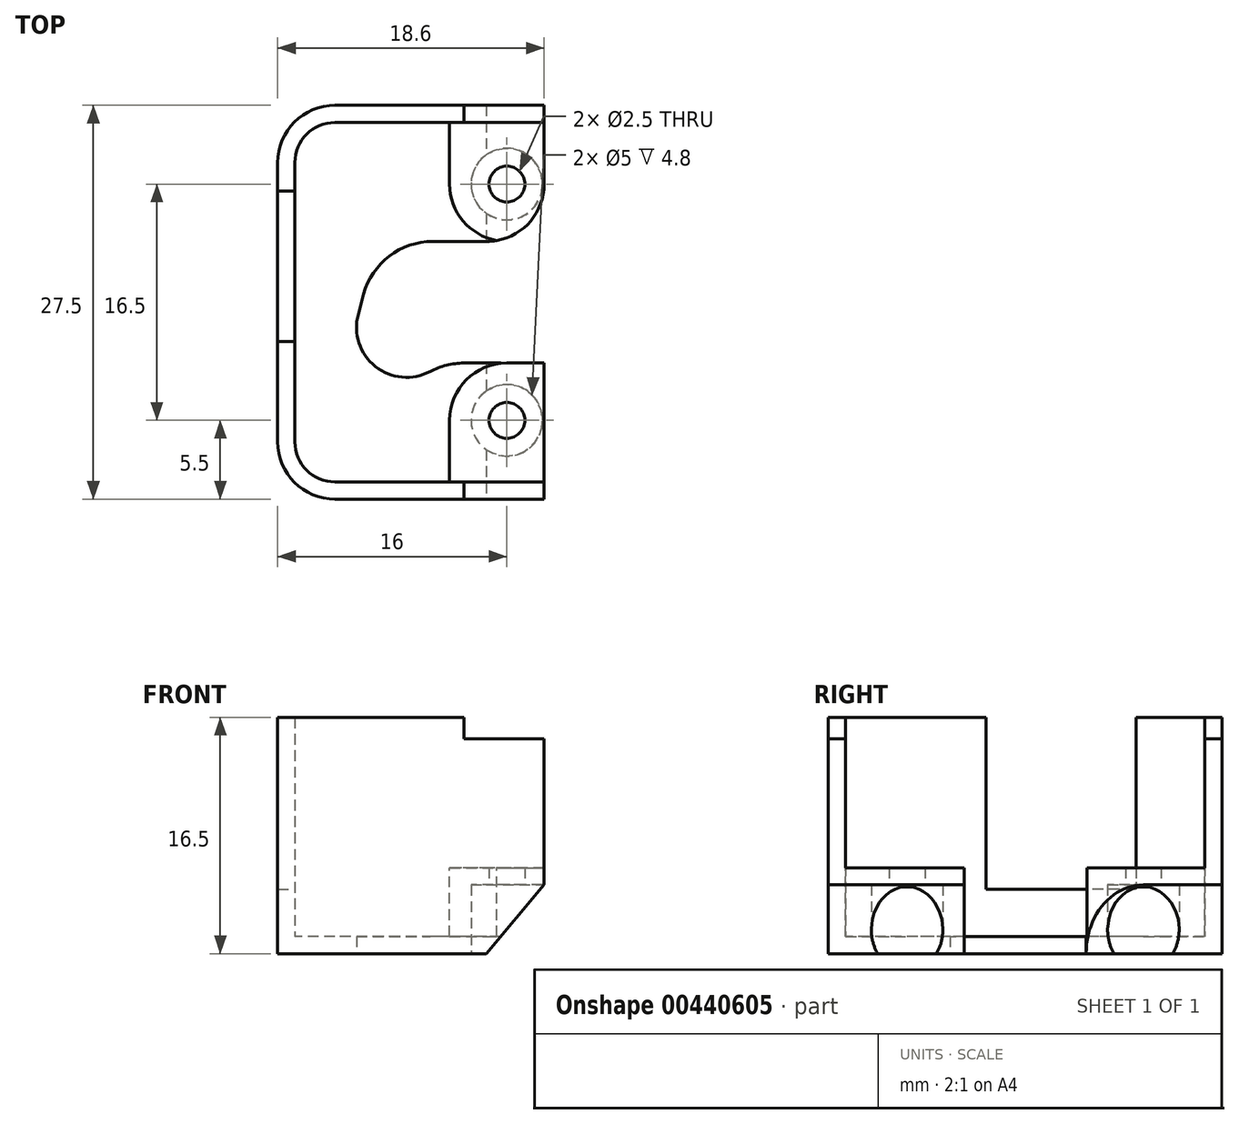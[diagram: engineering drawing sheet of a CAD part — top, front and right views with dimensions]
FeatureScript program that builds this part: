
annotation { "Feature Type Name" : "Feature", "Feature Type Description" : "" }
export const myFeature = defineFeature(function(context is Context, id is Id, definition is map)
    precondition{}
    {
        {
            var Q0;
            Q0=qCreatedBy(makeId("Top.planeOp"),FACE);
            var sketch = newSketch(context, id + "F0", { "sketchPlane" : qUnion([Q0])});
            skCircle(sketch, "E0", {"center": v(0, 8.25) * mm, "radius": 1.25 * mm});
            skCircle(sketch, "E1", {"center": v(0, -8.25) * mm, "radius": 1.25 * mm});
            skCircle(sketch, "E2", {"center": v(37.5, 11) * mm, "radius": 1.25 * mm});
            skCircle(sketch, "E3", {"center": v(37.5, -11) * mm, "radius": 1.25 * mm});
            skSolve(sketch);
        }
        {
            var Q0;
            Q0=qCreatedBy(makeId("Top.planeOp"),FACE);
            var sketch = newSketch(context, id + "F1", { "sketchPlane" : qUnion([Q0])});
            skLineSegment(sketch, "E4.bottom", {"start": v(-4, 12.25) * mm, "end": v(33.5, 12.25) * mm});
            skLineSegment(sketch, "E4.top", {"start": v(-4, -12.25) * mm, "end": v(33.5, -12.25) * mm});
            skLineSegment(sketch, "E4.left", {"start": v(-4, 12.25) * mm, "end": v(-4, -12.25) * mm});
            skLineSegment(sketch, "E4.right", {"start": v(43.5, 15) * mm, "end": v(43.5, -15) * mm});
            skCircle(sketch, "E5", {"center": v(37.5, 11) * mm, "radius": 2.5 * mm, "construction": true});
            skCircle(sketch, "E6", {"center": v(37.5, -11) * mm, "radius": 2.5 * mm, "construction": true});
            skCircle(sketch, "E7", {"center": v(0, 8.25) * mm, "radius": 2.5 * mm});
            skCircle(sketch, "E8", {"center": v(0, -8.25) * mm, "radius": 2.5 * mm});
            skLineSegment(sketch, "E9", {"start": v(33.5, 15) * mm, "end": v(43.5, 15) * mm});
            skLineSegment(sketch, "E10", {"start": v(33.5, -15) * mm, "end": v(43.5, -15) * mm});
            skLineSegment(sketch, "E11", {"start": v(33.5, 12.25) * mm, "end": v(33.5, 15) * mm});
            skLineSegment(sketch, "E12", {"start": v(33.5, -12.25) * mm, "end": v(33.5, -15) * mm});
            skSolve(sketch);
        }
        {
            var Q0;
            Q0=qCreatedBy(makeId("Top.planeOp"),FACE);
            var sketch = newSketch(context, id + "F2", { "sketchPlane" : qUnion([Q0])});
            skCircle(sketch, "E13", {"center": v(0, 8.25) * mm, "radius": 2.5 * mm, "construction": true});
            skLineSegment(sketch, "E14.bottom", {"start": v(2.6, 13.75) * mm, "end": v(-16, 13.75) * mm});
            skLineSegment(sketch, "E14.top", {"start": v(2.6, -13.75) * mm, "end": v(-16, -13.75) * mm});
            skLineSegment(sketch, "E14.left", {"start": v(2.6, 13.75) * mm, "end": v(2.6, 4.25) * mm});
            skLineSegment(sketch, "E14.right", {"start": v(-16, 13.75) * mm, "end": v(-16, -13.75) * mm});
            skLineSegment(sketch, "E15.bottom", {"start": v(2.6, -4.25) * mm, "end": v(-4.55, -4.25) * mm});
            skLineSegment(sketch, "E15.top", {"start": v(2.6, 4.25) * mm, "end": v(-9, 4.25) * mm});
            skLineSegment(sketch, "E16.trimOffspring", {"start": v(2.6, -4.25) * mm, "end": v(2.6, -13.75) * mm});
            skArc(sketch, "E17", {"start": v(-10.38, -0.83) * mm, "mid": v(-8.77, -4.77) * mm, "end": v(-4.55, -4.25) * mm});
            skLineSegment(sketch, "E18", {"start": v(-9, 4.25) * mm, "end": v(-10.38, -0.83) * mm});
            skSolve(sketch);
        }
        {
            var Q0;
            Q0=qCreatedBy(makeId("Top.planeOp"),FACE);
            var sketch = newSketch(context, id + "F3", { "sketchPlane" : qUnion([Q0])});
            skLineSegment(sketch, "E19.bottom", {"start": v(2.6, -4.25) * mm, "end": v(-5.4, -4.25) * mm});
            skLineSegment(sketch, "E19.top", {"start": v(2.6, 4.25) * mm, "end": v(-5.4, 4.25) * mm});
            skLineSegment(sketch, "E19.right", {"start": v(-5.4, -4.25) * mm, "end": v(-5.4, 4.25) * mm});
            skLineSegment(sketch, "E20", {"start": v(2.6, -4.25) * mm, "end": v(2.6, 4.25) * mm});
            skSolve(sketch);
        }
        {
            var Q0;
            Q0=makeQuery(id+"F2.imprint","IMPRINT",FACE,{"disambiguationData":[TD([[makeQuery(id+"F2.imprint","IMPRINT",EDGE,{"derivedFrom":sQuery(id+"F2.wireOp",EDGE,"E14.bottom")}),1.0]])]});
            var Q1;
            {var subQ0=sQuery(id+"F2.wireOp",EDGE,"E15.right");var subQ1=sQuery(id+"F2.wireOp",EDGE,"E15.bottom");var subQ2=makeQuery(id+"F2.imprint","INTERSECT",VERTEX,{"derivedFrom":[subQ1,subQ0]});Q1=makeQuery(id+"F2.imprint","IMPRINT",FACE,{"disambiguationData":[TD([[makeQuery(id+"F2.imprint","IMPRINT",EDGE,{"disambiguationData":[TD([[subQ2,1.0]])],"derivedFrom":subQ1}),-1.0]])]});}
            extrude(context, id + "F4", {"entities" : qUnion([Q0, Q1]), "depth" : 13.5 * mm, "hasSecondDirection" : true, "secondDirectionOppositeDirection" : true, "secondDirectionDepth" : 3 * mm});
        }
        {
            var Q0;
            Q0=makeQuery(id+"F4.opExtrude","SWEPT_EDGE",EDGE,{"disambiguationData":[OSD([sQuery(id+"F2.wireOp",EDGE,"E14.bottom"),sQuery(id+"F2.wireOp",EDGE,"E14.right")])]});
            var Q1;
            Q1=makeQuery(id+"F4.opExtrude","SWEPT_EDGE",EDGE,{"disambiguationData":[OSD([sQuery(id+"F2.wireOp",EDGE,"E14.top"),sQuery(id+"F2.wireOp",EDGE,"E14.right")])]});
            fillet(context, id + "F5", {"entities" : qUnion([Q0, Q1]), "radius" : 4 * mm, "tangentPropagation" : true, "allowEdgeOverflow" : false});
        }
        {
            var Q0;
            Q0=makeQuery(id+"F4.opExtrude","CAP_FACE",FACE,{"disambiguationData":[OSD([sQuery(id+"F2.wireOp",EDGE,"E14.bottom"),sQuery(id+"F2.wireOp",EDGE,"E14.top"),sQuery(id+"F2.wireOp",EDGE,"E14.left"),sQuery(id+"F2.wireOp",EDGE,"E14.right"),sQuery(id+"F2.wireOp",EDGE,"E15.bottom"),sQuery(id+"F2.wireOp",EDGE,"E15.top"),sQuery(id+"F2.wireOp",EDGE,"E15.right"),sQuery(id+"F2.wireOp",EDGE,"E16.trimOffspring")])],"isStart":false});
            var Q1;
            Q1=makeQuery(id+"F4.opExtrude","SWEPT_FACE",FACE,{"disambiguationData":[OSD([sQuery(id+"F2.wireOp",EDGE,"E14.left")])]});
            var Q2;
            Q2=makeQuery(id+"F4.opExtrude","SWEPT_FACE",FACE,{"disambiguationData":[OSD([sQuery(id+"F2.wireOp",EDGE,"E16.trimOffspring")])]});
            var Q3;
            Q3=makeQuery(id+"F4.opExtrude","SWEPT_FACE",FACE,{"disambiguationData":[OSD([sQuery(id+"F2.wireOp",EDGE,"E15.right")])]});
            var Q4;
            Q4=makeQuery(id+"F4.opExtrude","SWEPT_FACE",FACE,{"disambiguationData":[OSD([sQuery(id+"F2.wireOp",EDGE,"E15.bottom")])]});
            var Q5;
            Q5=makeQuery(id+"F4.opExtrude","SWEPT_FACE",FACE,{"disambiguationData":[OSD([sQuery(id+"F2.wireOp",EDGE,"E15.top")])]});
            var Q6;
            {var subQ1=sQuery(id+"F2.wireOp",EDGE,"E14.top");Q6=makeQuery(id+"F8.boolean.opBoolean","COPY",FACE,{"disambiguationData":[TD([makeQuery(id+"F4.opExtrude","SWEPT_FACE",FACE,{"disambiguationData":[OSD([subQ1])]})])],"derivedFrom":makeQuery(id+"F8.opExtrude","SWEPT_FACE",FACE,{"disambiguationData":[OSD([sQuery(id+"F7.wireOp",EDGE,"E21.right")])]})});}
            var Q7;
            {var subQ0=sQuery(id+"F2.wireOp",EDGE,"E14.bottom");Q7=makeQuery(id+"F8.boolean.opBoolean","COPY",FACE,{"disambiguationData":[TD([makeQuery(id+"F4.opExtrude","SWEPT_FACE",FACE,{"disambiguationData":[OSD([subQ0])]})])],"derivedFrom":makeQuery(id+"F8.opExtrude","SWEPT_FACE",FACE,{"disambiguationData":[OSD([sQuery(id+"F7.wireOp",EDGE,"E21.right")])]})});}
            var Q8;
            Q8=makeQuery(id+"F4.opExtrude","SWEPT_FACE",FACE,{"disambiguationData":[OSD([sQuery(id+"F2.wireOp",EDGE,"E17")])]});
            var Q9;
            Q9=makeQuery(id+"F4.opExtrude","SWEPT_FACE",FACE,{"disambiguationData":[OSD([sQuery(id+"F2.wireOp",EDGE,"E18")])]});
            shell(context, id + "F6", {"entities" : qUnion([Q0, Q1, Q2, Q3, Q4, Q5, Q6, Q7, Q8, Q9]), "thickness" : 1.2 * mm});
        }
        {
            var Q0;
            Q0=qCreatedBy(makeId("Front.planeOp"),FACE);
            var sketch = newSketch(context, id + "F7", { "sketchPlane" : qUnion([Q0])});
            skLineSegment(sketch, "E21.bottom", {"start": v(2.6, -3) * mm, "end": v(-4, -3) * mm});
            skLineSegment(sketch, "E21.top", {"start": v(2.6, 3) * mm, "end": v(-4, 3) * mm});
            skLineSegment(sketch, "E21.left", {"start": v(2.6, -3) * mm, "end": v(2.6, 3) * mm});
            skLineSegment(sketch, "E21.right", {"start": v(-4, -3) * mm, "end": v(-4, 3) * mm});
            skSolve(sketch);
        }
        {
            var Q0;
            Q0=makeQuery(id+"F7.imprint","IMPRINT",FACE,{"disambiguationData":[TD([[makeQuery(id+"F7.imprint","IMPRINT",EDGE,{"derivedFrom":sQuery(id+"F7.wireOp",EDGE,"E21.bottom")}),-1.0]])]});
            var Q1;
            Q1=makeQuery(id+"F4.opExtrude","SWEPT_FACE",FACE,{"disambiguationData":[OSD([sQuery(id+"F2.wireOp",EDGE,"E14.bottom")])]});
            var Q2;
            Q2=makeQuery(id+"F4.opExtrude","SWEPT_FACE",FACE,{"disambiguationData":[OSD([sQuery(id+"F2.wireOp",EDGE,"E14.top")])]});
            extrude(context, id + "F8", {"entities" : qUnion([Q0]), "operationType" : NewBodyOperationType.ADD, "endBound" : BoundingType.UP_TO_SURFACE, "oppositeDirection" : true, "endBoundEntityFace" : qUnion([Q1]), "depth" : 13 * mm, "hasSecondDirection" : true, "secondDirectionBound" : SecondDirectionBoundingType.UP_TO_SURFACE, "secondDirectionOppositeDirection" : false, "secondDirectionBoundEntityFace" : qUnion([Q2]), "secondDirectionDepth" : 25 * mm});
        }
        {
            var Q0;
            Q0=makeQuery(id+"F3.imprint","IMPRINT",FACE,{"disambiguationData":[TD([[makeQuery(id+"F3.imprint","IMPRINT",EDGE,{"derivedFrom":sQuery(id+"F3.wireOp",EDGE,"E19.bottom")}),-1.0]])]});
            extrude(context, id + "F9", {"entities" : qUnion([Q0]), "operationType" : NewBodyOperationType.REMOVE, "depth" : 4.5 * mm, "hasSecondDirection" : true, "secondDirectionOppositeDirection" : true, "secondDirectionDepth" : 4.3 * mm});
        }
        {
            var Q0;
            Q0=qCreatedBy(makeId("Right.planeOp"),FACE);
            var sketch = newSketch(context, id + "F10", { "sketchPlane" : qUnion([Q0])});
            skLineSegment(sketch, "E22.bottom", {"start": v(7.75, 19.94) * mm, "end": v(-2.75, 19.94) * mm});
            skLineSegment(sketch, "E22.top", {"start": v(7.75, 1.5) * mm, "end": v(-2.75, 1.5) * mm});
            skLineSegment(sketch, "E22.left", {"start": v(7.75, 19.94) * mm, "end": v(7.75, 1.5) * mm});
            skLineSegment(sketch, "E22.right", {"start": v(-2.75, 19.94) * mm, "end": v(-2.75, 1.5) * mm});
            skSolve(sketch);
        }
        {
            var Q0;
            Q0 = qSketchRegion(id + "F10", true);
            extrude(context, id + "F11", {"entities" : qUnion([Q0]), "operationType" : NewBodyOperationType.REMOVE, "oppositeDirection" : true, "depth" : 17.9 * mm, "hasSecondDirection" : true, "secondDirectionOppositeDirection" : true, "secondDirectionDepth" : 6.5 * mm});
        }
        {
            var Q0;
            Q0=makeQuery(id+"F9.boolean.opBoolean","COPY",EDGE,{"derivedFrom":makeQuery(id+"F9.opExtrude","SWEPT_EDGE",EDGE,{"disambiguationData":[OSD([sQuery(id+"F3.wireOp",EDGE,"E19.bottom"),sQuery(id+"F3.wireOp",EDGE,"E20")])]})});
            var Q1;
            Q1=makeQuery(id+"F9.boolean.opBoolean","INTERSECT",EDGE,{"derivedFrom":[makeQuery(id+"F8.opExtrude","SWEPT_FACE",FACE,{"disambiguationData":[OSD([sQuery(id+"F7.wireOp",EDGE,"E21.right")])]}),makeQuery(id+"F9.opExtrude","SWEPT_FACE",FACE,{"disambiguationData":[OSD([sQuery(id+"F3.wireOp",EDGE,"E19.bottom")])]})]});
            var Q2;
            Q2=makeQuery(id+"F9.boolean.opBoolean","INTERSECT",EDGE,{"derivedFrom":[makeQuery(id+"F8.opExtrude","SWEPT_FACE",FACE,{"disambiguationData":[OSD([sQuery(id+"F7.wireOp",EDGE,"E21.right")])]}),makeQuery(id+"F9.opExtrude","SWEPT_FACE",FACE,{"disambiguationData":[OSD([sQuery(id+"F3.wireOp",EDGE,"E19.top")])]})]});
            var Q3;
            Q3=makeQuery(id+"F9.boolean.opBoolean","COPY",EDGE,{"derivedFrom":makeQuery(id+"F9.opExtrude","SWEPT_EDGE",EDGE,{"disambiguationData":[OSD([sQuery(id+"F3.wireOp",EDGE,"E19.top"),sQuery(id+"F3.wireOp",EDGE,"E20")])]})});
            fillet(context, id + "F12", {"entities" : qUnion([Q0, Q1, Q2, Q3]), "radius" : 4 * mm, "tangentPropagation" : true, "allowEdgeOverflow" : false});
        }
        {
            var Q0;
            Q0=makeQuery(id+"F0.imprint","IMPRINT",FACE,{"disambiguationData":[TD([[makeQuery(id+"F0.imprint","IMPRINT",EDGE,{"derivedFrom":sQuery(id+"F0.wireOp",EDGE,"E1")}),1.0]])]});
            var Q1;
            Q1=makeQuery(id+"F0.imprint","IMPRINT",FACE,{"disambiguationData":[TD([[makeQuery(id+"F0.imprint","IMPRINT",EDGE,{"derivedFrom":sQuery(id+"F0.wireOp",EDGE,"E0")}),1.0]])]});
            extrude(context, id + "F13", {"entities" : qUnion([Q0, Q1]), "operationType" : NewBodyOperationType.REMOVE, "depth" : 7.9 * mm, "hasSecondDirection" : true, "secondDirectionOppositeDirection" : true, "secondDirectionDepth" : 7.1 * mm});
        }
        {
            var Q0;
            Q0=makeQuery(id+"F1.imprint","IMPRINT",FACE,{"disambiguationData":[TD([[makeQuery(id+"F1.imprint","IMPRINT",EDGE,{"derivedFrom":sQuery(id+"F1.wireOp",EDGE,"E8")}),1.0]])]});
            var Q1;
            Q1=makeQuery(id+"F1.imprint","IMPRINT",FACE,{"disambiguationData":[TD([[makeQuery(id+"F1.imprint","IMPRINT",EDGE,{"derivedFrom":sQuery(id+"F1.wireOp",EDGE,"E7")}),1.0]])]});
            extrude(context, id + "F14", {"entities" : qUnion([Q0, Q1]), "operationType" : NewBodyOperationType.REMOVE, "depth" : 1.8 * mm, "hasSecondDirection" : true, "secondDirectionOppositeDirection" : true, "secondDirectionDepth" : 4.3 * mm});
        }
        {
            var Q0;
            Q0=makeQuery(id+"F4.opExtrude","SWEPT_EDGE",EDGE,{"disambiguationData":[OSD([sQuery(id+"F2.wireOp",EDGE,"E15.bottom"),sQuery(id+"F2.wireOp",EDGE,"E17")])]});
            var Q1;
            Q1=makeQuery(id+"F4.opExtrude","SWEPT_EDGE",EDGE,{"disambiguationData":[OSD([sQuery(id+"F2.wireOp",EDGE,"E15.top"),sQuery(id+"F2.wireOp",EDGE,"E18")])]});
            var Q2;
            Q2=makeQuery(id+"F4.opExtrude","SWEPT_EDGE",EDGE,{"disambiguationData":[OSD([sQuery(id+"F2.wireOp",EDGE,"E15.bottom"),sQuery(id+"F2.wireOp",EDGE,"E17")])]});
            fillet(context, id + "F15", {"entities" : qUnion([Q0, Q1, Q2]), "radius" : 5 * mm, "tangentPropagation" : true, "allowEdgeOverflow" : false});
        }
        {
            var Q0;
            Q0=qCreatedBy(makeId("Front.planeOp"),FACE);
            var sketch = newSketch(context, id + "F16", { "sketchPlane" : qUnion([Q0])});
            skLineSegment(sketch, "E23", {"start": v(-4, -6.07) * mm, "end": v(2.6, 1.8) * mm});
            skLineSegment(sketch, "E24", {"start": v(2.6, 1.8) * mm, "end": v(8.7, -6.26) * mm});
            skLineSegment(sketch, "E25", {"start": v(8.7, -6.26) * mm, "end": v(2.4, -10.94) * mm});
            skLineSegment(sketch, "E26", {"start": v(2.4, -10.94) * mm, "end": v(-4, -6.07) * mm});
            skSolve(sketch);
        }
        {
            var Q0;
            Q0=makeQuery(id+"F16.imprint","IMPRINT",FACE,{"disambiguationData":[TD([[makeQuery(id+"F16.imprint","IMPRINT",EDGE,{"derivedFrom":sQuery(id+"F16.wireOp",EDGE,"E23")}),-1.0]])]});
            extrude(context, id + "F17", {"entities" : qUnion([Q0]), "operationType" : NewBodyOperationType.REMOVE, "depth" : 16 * mm, "hasSecondDirection" : true, "secondDirectionOppositeDirection" : true, "secondDirectionDepth" : 16.1 * mm});
        }
        {
            var Q0;
            Q0=qCreatedBy(makeId("Front.planeOp"),FACE);
            var sketch = newSketch(context, id + "F18", { "sketchPlane" : qUnion([Q0])});
            skLineSegment(sketch, "E27.bottom", {"start": v(2.6, 15) * mm, "end": v(-3, 15) * mm});
            skLineSegment(sketch, "E27.top", {"start": v(2.6, 12) * mm, "end": v(-3, 12) * mm});
            skLineSegment(sketch, "E27.left", {"start": v(2.6, 15) * mm, "end": v(2.6, 12) * mm});
            skLineSegment(sketch, "E27.right", {"start": v(-3, 15) * mm, "end": v(-3, 12) * mm});
            skSolve(sketch);
        }
        {
            var Q0;
            Q0=makeQuery(id+"F18.imprint","IMPRINT",FACE,{"disambiguationData":[TD([[makeQuery(id+"F18.imprint","IMPRINT",EDGE,{"derivedFrom":sQuery(id+"F18.wireOp",EDGE,"E27.bottom")}),1.0]])]});
            extrude(context, id + "F19", {"entities" : qUnion([Q0]), "operationType" : NewBodyOperationType.REMOVE, "depth" : 25 * mm, "hasSecondDirection" : true, "secondDirectionOppositeDirection" : true, "secondDirectionDepth" : 25 * mm});
        }
    });
